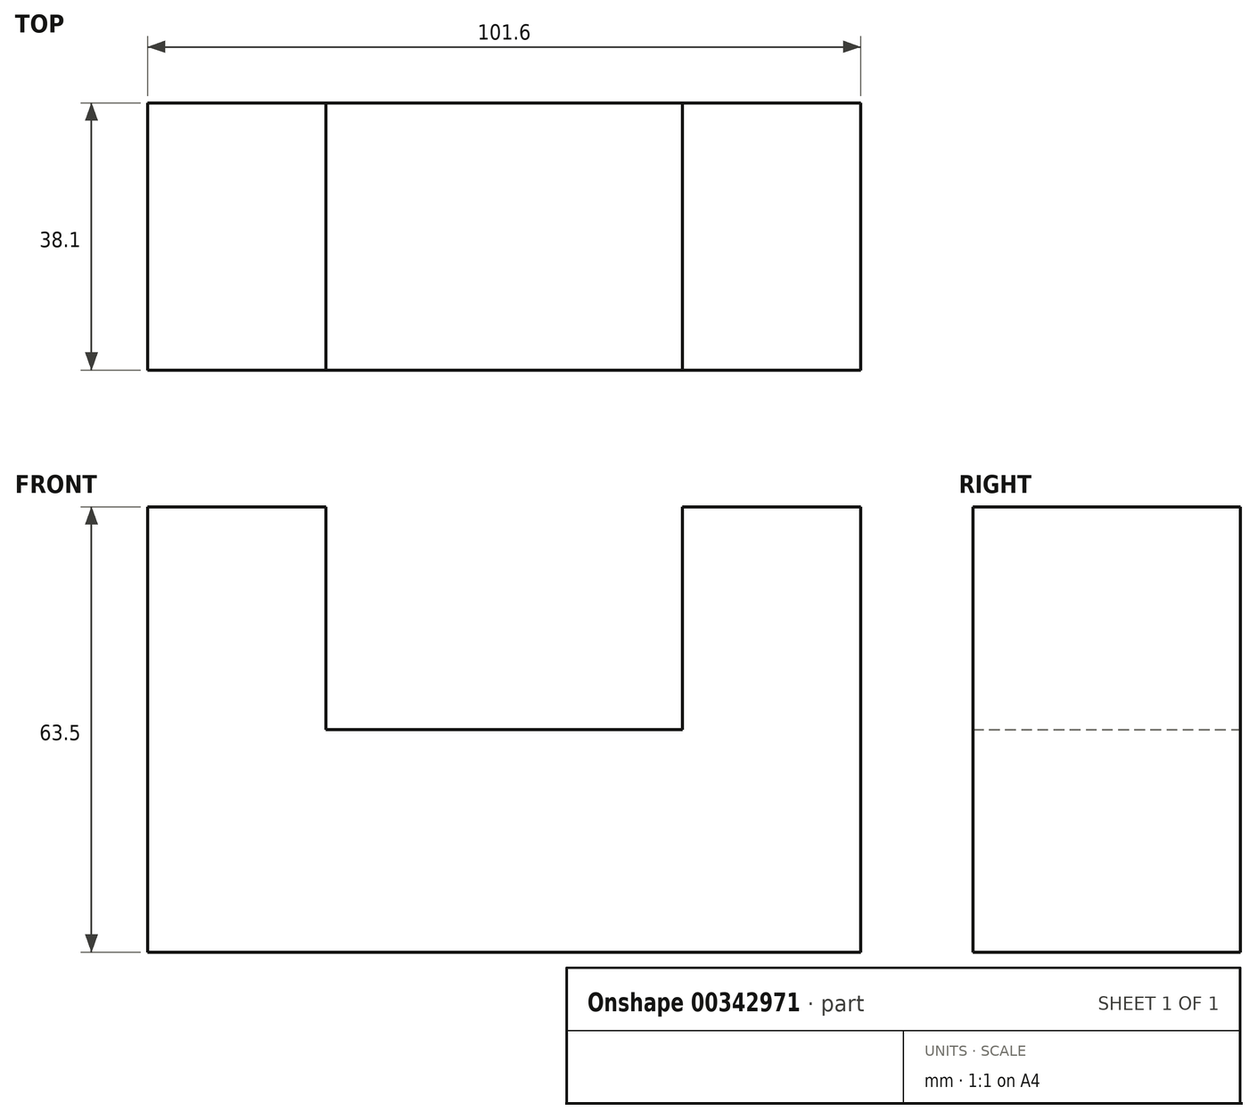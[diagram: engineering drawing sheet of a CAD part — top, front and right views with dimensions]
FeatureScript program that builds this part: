
annotation { "Feature Type Name" : "Feature", "Feature Type Description" : "" }
export const myFeature = defineFeature(function(context is Context, id is Id, definition is map)
    precondition{}
    {
        {
            var Q0;
            Q0=qCreatedBy(makeId("Front.planeOp"),FACE);
            var sketch = newSketch(context, id + "F0", { "sketchPlane" : qUnion([Q0])});
            skLineSegment(sketch, "E0", {"start": v(54.67, 17.61) * mm, "end": v(54.67, -45.89) * mm});
            skLineSegment(sketch, "E1", {"start": v(54.67, -45.89) * mm, "end": v(-46.93, -45.89) * mm});
            skLineSegment(sketch, "E2", {"start": v(-46.93, -45.89) * mm, "end": v(-46.93, 17.61) * mm});
            skLineSegment(sketch, "E3", {"start": v(-46.93, 17.61) * mm, "end": v(-21.53, 17.61) * mm});
            skLineSegment(sketch, "E4", {"start": v(-21.53, 17.61) * mm, "end": v(-21.53, -14.14) * mm});
            skLineSegment(sketch, "E5", {"start": v(-21.53, -14.14) * mm, "end": v(29.27, -14.14) * mm});
            skLineSegment(sketch, "E6", {"start": v(29.27, -14.14) * mm, "end": v(29.27, 17.61) * mm});
            skLineSegment(sketch, "E7", {"start": v(29.27, 17.61) * mm, "end": v(54.67, 17.61) * mm});
            skSolve(sketch);
        }
        {
            var Q0;
            Q0 = qSketchRegion(id + "F0", true);
            extrude(context, id + "F1", {"entities" : qUnion([Q0]), "depth" : 38.1 * mm});
        }
    });
